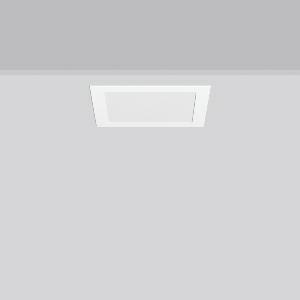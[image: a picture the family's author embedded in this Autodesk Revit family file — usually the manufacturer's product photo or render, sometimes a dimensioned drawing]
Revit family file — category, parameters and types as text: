
# Revit family: toledo_flat_square_e_901487_002_76_e74d
name_source: partatom
category: Lighting Fixtures
units: mm (PartAtom-declared; Revit-internal decimal feet)

## family parameters
Cut with Voids When Loaded = No
Host = Face
Light Source = No
Part Type = Normal
Room Calculation Point = No
Round Connector Dimension = Use Diameter
Shared = No

## types (1)
- TOLEDO FLAT square E (1 x LED Modul 830, 1650 lm, 3000)
    Apparent Load = 17 VA
    CIE Flux Codes = 48 80 96 100 100
    Color Rendering = 80
    Color Temperature = 3000
    Default Elevation = 1800 mm
    Description = Series: TOLEDO FLAT square
Ultra thin recessed downlight. Housing: die-cast aluminium. Light guide and diffuser made of non-yellowing PMMA, opal matt. Ceiling installation with spring system. Mounting depth depends on ceiling strength. Suitable for through-wiring with separately available accessories. Surface mounted housing as accessory for all sizes. Retrofittable decorative cylinders made of chintz fabric as accessory, optional with satin finish plastic diffuser. Through-wiring box (5 pole) available as accessory. 
Colour: white
Length: 225 mm
Width: 225 mm
Height: 3 mm
Cut-out length: 208 mm
Cut-out width: 208 mm
Recess height: 31-56 mm
Luminaire: recess height: 31-51 mm
Lamp: LED
Socket: without socket
Colour temperature: 3000K
Colour rendering index (CRI): 80
System power: 17 W
Rated luminous flux: 1650 lm
Luminous efficiency: 97 lm/W
Control gear: Converter, dimmable, DALI
Protection class: II
Type of protection: IP 54
    Height = 0 mm  [stored 0 ft]
    Lamp = 1 x LED Modul 830
    Lamp Light Flux = 1650 lm
    Lamp count = 1
    Length = 225 mm
    Lifetime = 50000 h
    Luminous efficacy = 97 lm/W
    Manufacturer = RZB
    ModVariant = No
    Model = 901487.002.76
    Mounting Place = Ceiling
    Mounting Type = Recessed
    Number of Poles = 1
    OnlyDefault = Yes
    Power Factor = 1
    Product Name = TOLEDO FLAT square E
    Product group = Recessed downlights
    ProductGroupID = 402
    Protection Class = Protection class II
    Protection Degree = IP 20
    RLX_Detail_Level = 1
    RLX_Emergency_Light_Flux = 0 lm
    RLX_Emergency_Type = 0
    RLX_Emergency_Type_DB = No
    RlxData = <blob elided: 58853 chars, md5=ca68647c>
    Socket = socket
    Standby Power = 0 W
    System Light Flux = 1650 lm
    System Power = 17 W
    Type Comments = Product without accessories
    Type Image = 901487.002.jpg
    URL = http://relux.com
    VarID = ---
    Voltage = 230 V
    Voltage Range = 220-240 V
    Weight = 0.00 kg
    Width = 225 mm

note: [stored X ft] marks values corroborated as IEEE doubles in the binary element streams (Revit-internal decimal feet)

## geometry (parser evidence)
native form markers: Blend x4, Sweep x11
no freeform markers — native parametric forms only
